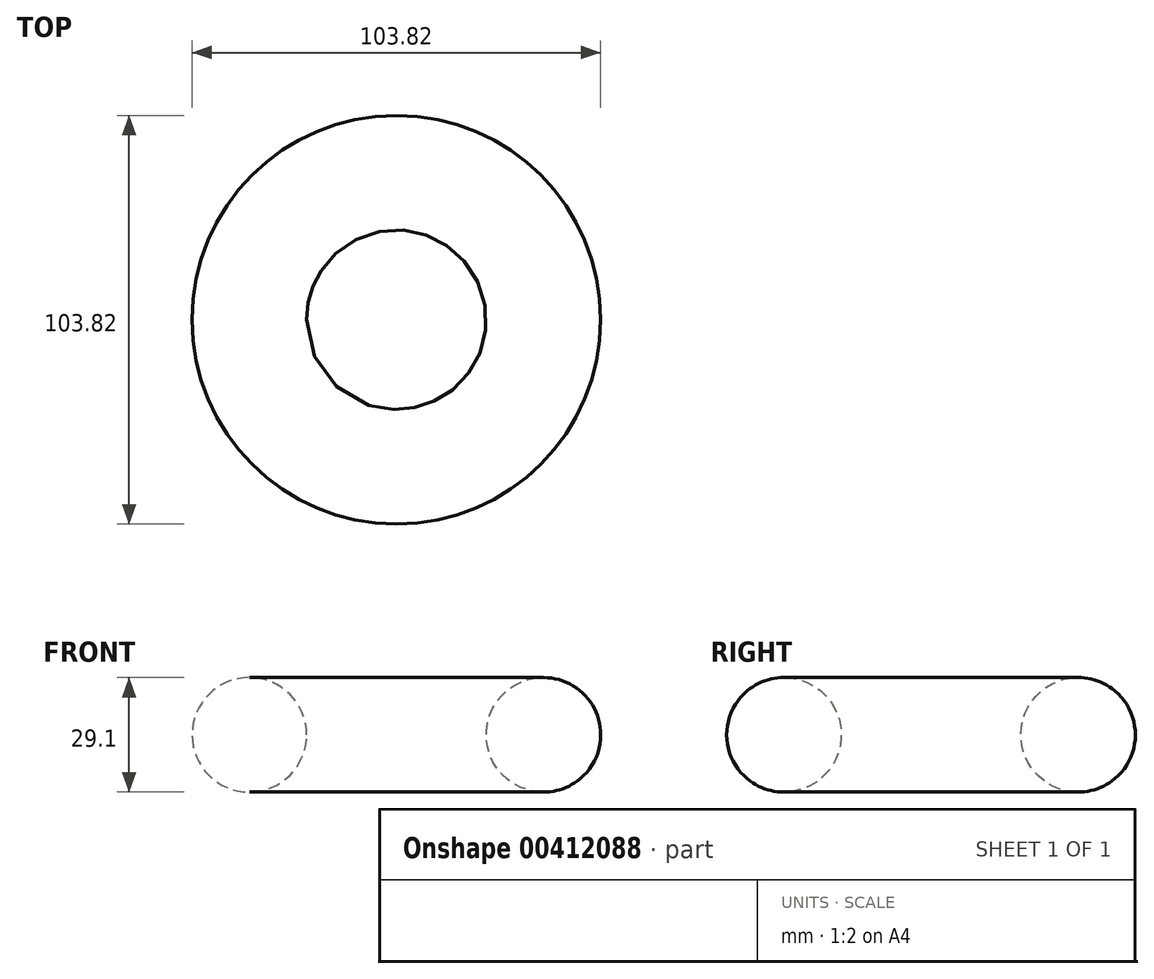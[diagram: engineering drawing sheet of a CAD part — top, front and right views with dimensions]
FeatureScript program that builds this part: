
annotation { "Feature Type Name" : "Feature", "Feature Type Description" : "" }
export const myFeature = defineFeature(function(context is Context, id is Id, definition is map)
    precondition{}
    {
        {
            var Q0;
            Q0=qCreatedBy(makeId("Front.planeOp"),FACE);
            var sketch = newSketch(context, id + "F0", { "sketchPlane" : qUnion([Q0])});
            skCircle(sketch, "E0", {"center": v(37.36, 0) * mm, "radius": 14.55 * mm});
            skSolve(sketch);
        }
        {
            var Q0;
            Q0=qCreatedBy(makeId("Front.planeOp"),FACE);
            var sketch = newSketch(context, id + "F1", { "sketchPlane" : qUnion([Q0])});
            skLineSegment(sketch, "E1", {"start": v(0, 73) * mm, "end": v(0, -32.13) * mm});
            skSolve(sketch);
        }
        {
            var Q0;
            Q0=sQuery(id+"F0.wireOp",EDGE,"E0");
            var Q1;
            Q1=sQuery(id+"F1.wireOp",EDGE,"E1");
            revolve(context, id + "F2", {"bodyType" : ToolBodyType.SURFACE, "surfaceEntities" : qUnion([Q0]), "axis" : qUnion([Q1]), "revolveType" : RevolveType.FULL});
        }
    });
